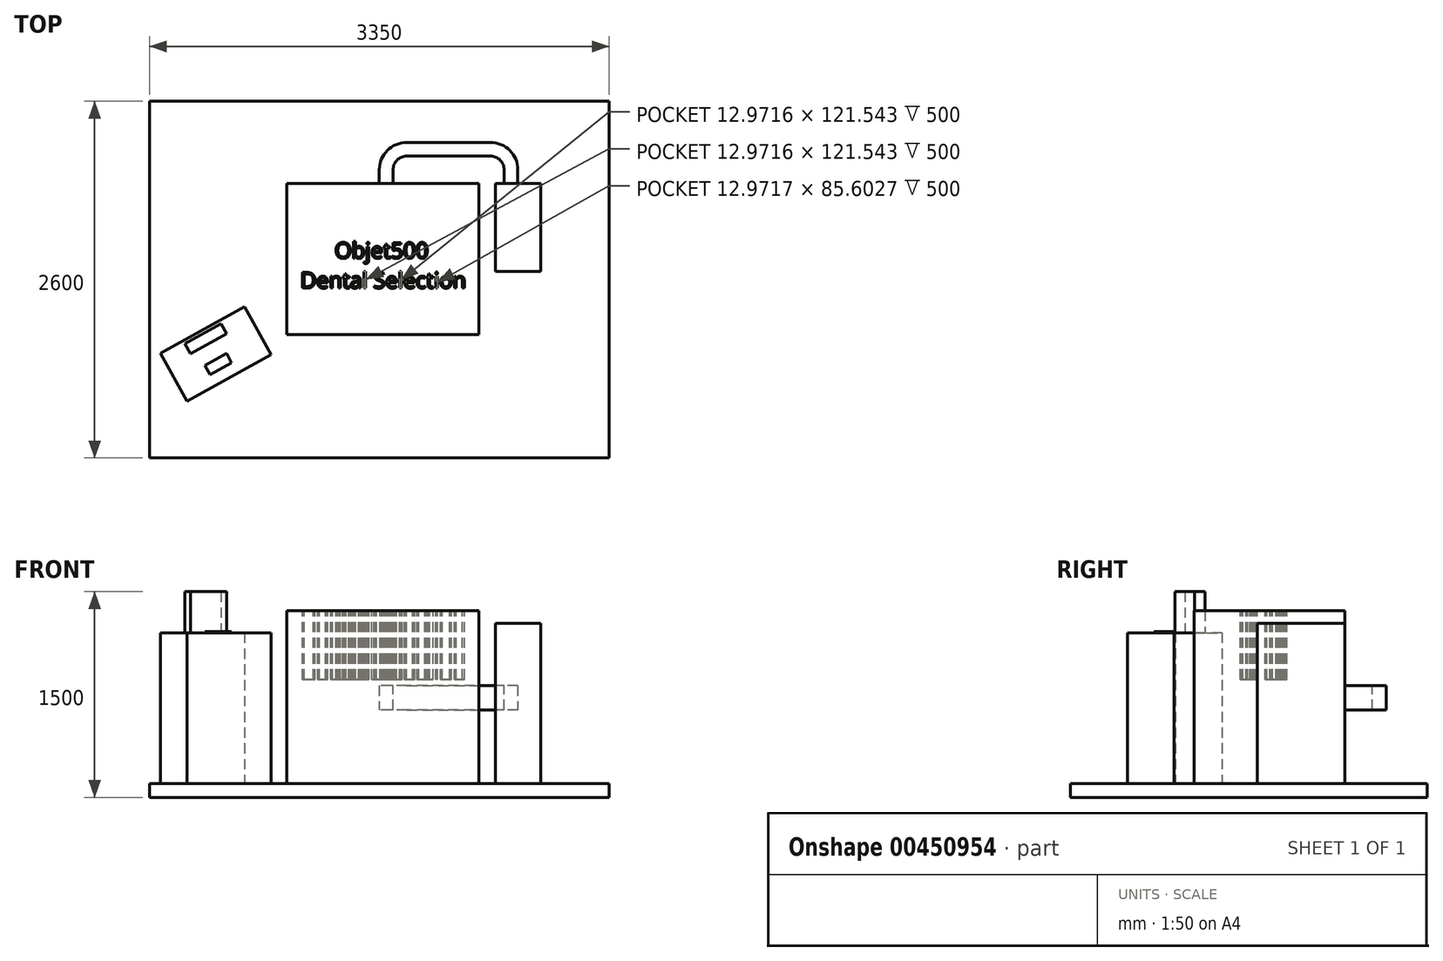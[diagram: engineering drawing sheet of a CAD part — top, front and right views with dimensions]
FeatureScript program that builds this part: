
annotation { "Feature Type Name" : "Feature", "Feature Type Description" : "" }
export const myFeature = defineFeature(function(context is Context, id is Id, definition is map)
    precondition{}
    {
        {
            var Q0;
            Q0=qCreatedBy(makeId("Top.planeOp"),FACE);
            var sketch = newSketch(context, id + "F0", { "sketchPlane" : qUnion([Q0])});
            skLineSegment(sketch, "E0.bottom", {"start": v(1675, -1300) * mm, "end": v(-1675, -1300) * mm});
            skLineSegment(sketch, "E0.top", {"start": v(1675, 1300) * mm, "end": v(-1675, 1300) * mm});
            skLineSegment(sketch, "E0.left", {"start": v(1675, -1300) * mm, "end": v(1675, 1300) * mm});
            skLineSegment(sketch, "E0.right", {"start": v(-1675, -1300) * mm, "end": v(-1675, 1300) * mm});
            skPoint(sketch, "E0.middle", {"position": v(0, 0) * mm});
            skSolve(sketch);
        }
        {
            var Q0;
            Q0 = qSketchRegion(id + "F0", true);
            extrude(context, id + "F1", {"entities" : qUnion([Q0]), "depth" : 100 * mm});
        }
        {
            var Q0;
            Q0=makeQuery(id+"F1.opExtrude","CAP_FACE",FACE,{"disambiguationData":[OSD([sQuery(id+"F0.wireOp",EDGE,"E0.bottom"),sQuery(id+"F0.wireOp",EDGE,"E0.top"),sQuery(id+"F0.wireOp",EDGE,"E0.left"),sQuery(id+"F0.wireOp",EDGE,"E0.right")])],"isStart":false});
            var sketch = newSketch(context, id + "F2", { "sketchPlane" : qUnion([Q0])});
            skLineSegment(sketch, "E1.bottom", {"start": v(725, -400) * mm, "end": v(-675, -400) * mm});
            skLineSegment(sketch, "E1.top", {"start": v(725, 700) * mm, "end": v(-675, 700) * mm});
            skLineSegment(sketch, "E1.left", {"start": v(725, -400) * mm, "end": v(725, 700) * mm});
            skLineSegment(sketch, "E1.right", {"start": v(-675, -400) * mm, "end": v(-675, 700) * mm});
            skSolve(sketch);
        }
        {
            var Q0;
            Q0 = qSketchRegion(id + "F2", true);
            extrude(context, id + "F3", {"entities" : qUnion([Q0]), "operationType" : NewBodyOperationType.ADD, "depth" : 1260 * mm});
        }
        {
            var Q0;
            Q0=makeQuery(id+"F1.opExtrude","CAP_FACE",FACE,{"disambiguationData":[OSD([sQuery(id+"F0.wireOp",EDGE,"E0.bottom"),sQuery(id+"F0.wireOp",EDGE,"E0.top"),sQuery(id+"F0.wireOp",EDGE,"E0.left"),sQuery(id+"F0.wireOp",EDGE,"E0.right")])],"isStart":false});
            var sketch = newSketch(context, id + "F4", { "sketchPlane" : qUnion([Q0])});
            skLineSegment(sketch, "E2.bottom", {"start": v(845, 700) * mm, "end": v(1175, 700) * mm});
            skLineSegment(sketch, "E2.top", {"start": v(845, 60) * mm, "end": v(1175, 60) * mm});
            skLineSegment(sketch, "E2.left", {"start": v(845, 700) * mm, "end": v(845, 60) * mm});
            skLineSegment(sketch, "E2.right", {"start": v(1175, 700) * mm, "end": v(1175, 60) * mm});
            skSolve(sketch);
        }
        {
            var Q0;
            Q0 = qSketchRegion(id + "F4", true);
            extrude(context, id + "F5", {"entities" : qUnion([Q0]), "operationType" : NewBodyOperationType.ADD, "depth" : 1170 * mm});
        }
        {
            var Q0;
            Q0=makeQuery(id+"F5.opExtrude","SWEPT_FACE",FACE,{"disambiguationData":[OSD([sQuery(id+"F4.wireOp",EDGE,"E2.bottom")])]});
            var sketch = newSketch(context, id + "F6", { "sketchPlane" : qUnion([Q0])});
            skLineSegment(sketch, "E3.bottom", {"start": v(-845, 814.44) * mm, "end": v(0, 814.44) * mm});
            skLineSegment(sketch, "E3.top", {"start": v(-845, 637.59) * mm, "end": v(0, 637.59) * mm});
            skLineSegment(sketch, "E3.left", {"start": v(-845, 814.44) * mm, "end": v(-845, 637.59) * mm});
            skLineSegment(sketch, "E3.right", {"start": v(0, 814.44) * mm, "end": v(0, 637.59) * mm});
            skPoint(sketch, "E4.oppositeSnap0", {"position": v(-1010, 100) * mm});
            skLineSegment(sketch, "E4.bottom", {"start": v(-845, 814.44) * mm, "end": v(-1010, 814.44) * mm});
            skLineSegment(sketch, "E4.top", {"start": v(-845, 637.59) * mm, "end": v(-1010, 637.59) * mm});
            skLineSegment(sketch, "E4.right", {"start": v(-1010, 814.44) * mm, "end": v(-1010, 637.59) * mm});
            skSolve(sketch);
        }
        {
            var Q0;
            Q0 = qSketchRegion(id + "F6", true);
            extrude(context, id + "F7", {"entities" : qUnion([Q0]), "operationType" : NewBodyOperationType.ADD, "depth" : 300 * mm});
        }
        {
            var Q0;
            Q0=makeQuery(id+"F7.opExtrude","CAP_EDGE",EDGE,{"disambiguationData":[OSD([sQuery(id+"F6.wireOp",EDGE,"E4.right")])],"isStart":false});
            var Q1;
            Q1=makeQuery(id+"F7.opExtrude","CAP_EDGE",EDGE,{"disambiguationData":[OSD([sQuery(id+"F6.wireOp",EDGE,"E3.right")])],"isStart":false});
            fillet(context, id + "F8", {"entities" : qUnion([Q0, Q1]), "radius" : 200 * mm, "tangentPropagation" : true, "allowEdgeOverflow" : false});
        }
        {
            var Q0;
            Q0=makeQuery(id+"F7.opExtrude","SWEPT_FACE",FACE,{"disambiguationData":[OSD([sQuery(id+"F6.wireOp",EDGE,"E3.bottom"),sQuery(id+"F6.wireOp",EDGE,"E4.bottom")])]});
            var sketch = newSketch(context, id + "F9", { "sketchPlane" : qUnion([Q0])});
            skArc(sketch, "E5", {"start": v(200, 900) * mm, "mid": v(129.29, 870.71) * mm, "end": v(100, 800) * mm});
            skArc(sketch, "E6", {"start": v(910, 800) * mm, "mid": v(880.71, 870.71) * mm, "end": v(810, 900) * mm});
            skLineSegment(sketch, "E7", {"start": v(100, 800) * mm, "end": v(100, 700) * mm});
            skLineSegment(sketch, "E8", {"start": v(200, 900) * mm, "end": v(810, 900) * mm});
            skLineSegment(sketch, "E9", {"start": v(910, 800) * mm, "end": v(910, 700) * mm});
            skSolve(sketch);
        }
        {
            var Q0;
            Q0 = qSketchRegion(id + "F9", true);
            var Q1;
            Q1=makeQuery(id+"F9.imprint","IMPRINT",FACE,{"disambiguationData":[TD([[makeQuery(id+"F9.imprint","IMPRINT",EDGE,{"derivedFrom":sQuery(id+"F9.wireOp",EDGE,"E5")}),1.0]])]});
            extrude(context, id + "F10", {"entities" : qUnion([Q0, Q1]), "operationType" : NewBodyOperationType.REMOVE, "oppositeDirection" : true, "depth" : 439 * mm});
        }
        {
            var Q0;
            Q0=makeQuery(id+"F1.opExtrude","CAP_FACE",FACE,{"disambiguationData":[OSD([sQuery(id+"F0.wireOp",EDGE,"E0.bottom"),sQuery(id+"F0.wireOp",EDGE,"E0.top"),sQuery(id+"F0.wireOp",EDGE,"E0.left"),sQuery(id+"F0.wireOp",EDGE,"E0.right")])],"isStart":false});
            var sketch = newSketch(context, id + "F11", { "sketchPlane" : qUnion([Q0])});
            skLineSegment(sketch, "E10", {"start": v(-1595.84, -536.88) * mm, "end": v(-983.93, -196.93) * mm});
            skLineSegment(sketch, "E11", {"start": v(-983.93, -196.93) * mm, "end": v(-789.68, -546.6) * mm});
            skLineSegment(sketch, "E12", {"start": v(-789.68, -546.6) * mm, "end": v(-1401.59, -886.55) * mm});
            skLineSegment(sketch, "E13", {"start": v(-1401.59, -886.55) * mm, "end": v(-1595.84, -536.88) * mm});
            skSolve(sketch);
        }
        {
            var Q0;
            Q0 = qSketchRegion(id + "F11", true);
            extrude(context, id + "F12", {"entities" : qUnion([Q0]), "operationType" : NewBodyOperationType.ADD, "depth" : 1100 * mm});
        }
        {
            var Q0;
            Q0=makeQuery(id+"F12.opExtrude","CAP_FACE",FACE,{"disambiguationData":[OSD([sQuery(id+"F11.wireOp",EDGE,"E10"),sQuery(id+"F11.wireOp",EDGE,"E11"),sQuery(id+"F11.wireOp",EDGE,"E12"),sQuery(id+"F11.wireOp",EDGE,"E13")])],"isStart":false});
            var sketch = newSketch(context, id + "F13", { "sketchPlane" : qUnion([Q0])});
            skLineSegment(sketch, "E14", {"start": v(-1416.33, -466.21) * mm, "end": v(-1154.09, -320.52) * mm});
            skLineSegment(sketch, "E15", {"start": v(-1154.09, -320.52) * mm, "end": v(-1112.52, -395.35) * mm});
            skLineSegment(sketch, "E16", {"start": v(-1112.52, -395.35) * mm, "end": v(-1374.76, -541.04) * mm});
            skLineSegment(sketch, "E17", {"start": v(-1374.76, -541.04) * mm, "end": v(-1416.33, -466.21) * mm});
            skSolve(sketch);
        }
        {
            var Q0;
            Q0 = qSketchRegion(id + "F13", true);
            extrude(context, id + "F14", {"entities" : qUnion([Q0]), "operationType" : NewBodyOperationType.ADD, "depth" : 300 * mm});
        }
        {
            var Q0;
            Q0 = qSketchRegion(id + "F13", true);
            extrude(context, id + "F15", {"entities" : qUnion([Q0]), "operationType" : NewBodyOperationType.ADD, "depth" : 300 * mm});
        }
        {
            var Q0;
            Q0=makeQuery(id+"F12.opExtrude","CAP_FACE",FACE,{"disambiguationData":[OSD([sQuery(id+"F11.wireOp",EDGE,"E10"),sQuery(id+"F11.wireOp",EDGE,"E11"),sQuery(id+"F11.wireOp",EDGE,"E12"),sQuery(id+"F11.wireOp",EDGE,"E13")])],"isStart":false});
            var sketch = newSketch(context, id + "F16", { "sketchPlane" : qUnion([Q0])});
            skLineSegment(sketch, "E18", {"start": v(-1269.99, -624.83) * mm, "end": v(-1113.9, -538.1) * mm});
            skLineSegment(sketch, "E19", {"start": v(-1113.9, -538.1) * mm, "end": v(-1076.13, -606.08) * mm});
            skLineSegment(sketch, "E20", {"start": v(-1076.13, -606.08) * mm, "end": v(-1232.22, -692.8) * mm});
            skLineSegment(sketch, "E21", {"start": v(-1232.22, -692.8) * mm, "end": v(-1269.99, -624.83) * mm});
            skSolve(sketch);
        }
        {
            var Q0;
            Q0 = qSketchRegion(id + "F16", true);
            extrude(context, id + "F17", {"entities" : qUnion([Q0]), "operationType" : NewBodyOperationType.ADD, "depth" : 10 * mm});
        }
        {
            var Q0;
            Q0=makeQuery(id+"F3.opExtrude","CAP_FACE",FACE,{"disambiguationData":[OSD([sQuery(id+"F2.wireOp",EDGE,"E1.bottom"),sQuery(id+"F2.wireOp",EDGE,"E1.top"),sQuery(id+"F2.wireOp",EDGE,"E1.left"),sQuery(id+"F2.wireOp",EDGE,"E1.right")])],"isStart":false});
            var sketch = newSketch(context, id + "F18", { "sketchPlane" : qUnion([Q0])});
            skText(sketch, "E22", { "text": "      Objet500\nDental Selection ", "fontName": "OpenSans-Regular.ttf"});
            const initialGuessF18  = {"E22": [-0.575, 0.15557, 1, 0, 0.11517]};
            skSetInitialGuess(sketch, initialGuessF18);
            skSolve(sketch);
        }
        {
            var Q0;
            Q0 = qSketchRegion(id + "F18", true);
            extrude(context, id + "F19", {"entities" : qUnion([Q0]), "operationType" : NewBodyOperationType.REMOVE, "oppositeDirection" : true, "depth" : 500 * mm});
        }
    });
